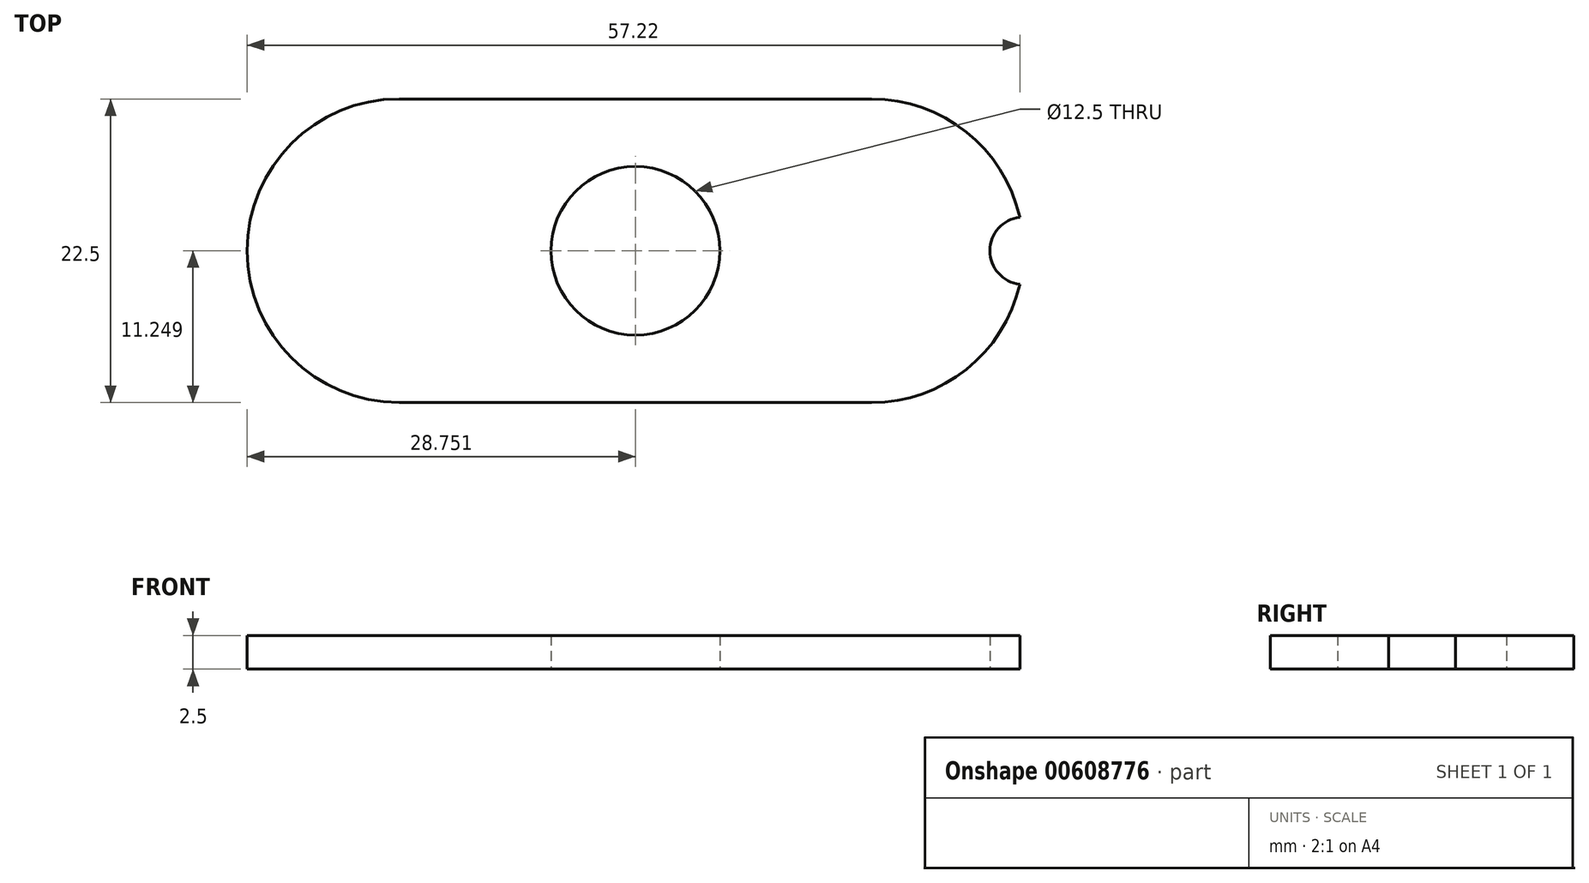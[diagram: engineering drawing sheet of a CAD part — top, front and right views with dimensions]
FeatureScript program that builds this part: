
annotation { "Feature Type Name" : "Feature", "Feature Type Description" : "" }
export const myFeature = defineFeature(function(context is Context, id is Id, definition is map)
    precondition{}
    {
        {
            var Q0;
            Q0=qCreatedBy(makeId("Top.planeOp"),FACE);
            var sketch = newSketch(context, id + "F0", { "sketchPlane" : qUnion([Q0])});
            skLineSegment(sketch, "E0.bottom", {"start": v(-28.55, -39.14) * mm, "end": v(6.45, -39.14) * mm});
            skLineSegment(sketch, "E0.top", {"start": v(-28.55, -16.64) * mm, "end": v(6.45, -16.64) * mm});
            skArc(sketch, "E1", {"start": v(6.45, -39.14) * mm, "mid": v(17.7, -27.9) * mm, "end": v(6.45, -16.64) * mm});
            skArc(sketch, "E2", {"start": v(-28.55, -16.64) * mm, "mid": v(-39.8, -27.9) * mm, "end": v(-28.55, -39.14) * mm});
            skCircle(sketch, "E3", {"center": v(-11.05, -27.9) * mm, "radius": 6.25 * mm});
            skPoint(sketch, "E3.centerSnap0", {"position": v(-11.05, -16.64) * mm});
            skCircle(sketch, "E4", {"center": v(17.7, -27.9) * mm, "radius": 2.5 * mm});
            skSolve(sketch);
        }
        {
            var Q0;
            Q0=makeQuery(id+"F0.imprint","IMPRINT",FACE,{"disambiguationData":[TD([[makeQuery(id+"F0.imprint","IMPRINT",EDGE,{"derivedFrom":sQuery(id+"F0.wireOp",EDGE,"E0.bottom")}),1.0]])]});
            extrude(context, id + "F1", {"entities" : qUnion([Q0]), "depth" : 2.5 * mm, "offsetDistance" : 25 * mm});
        }
    });
